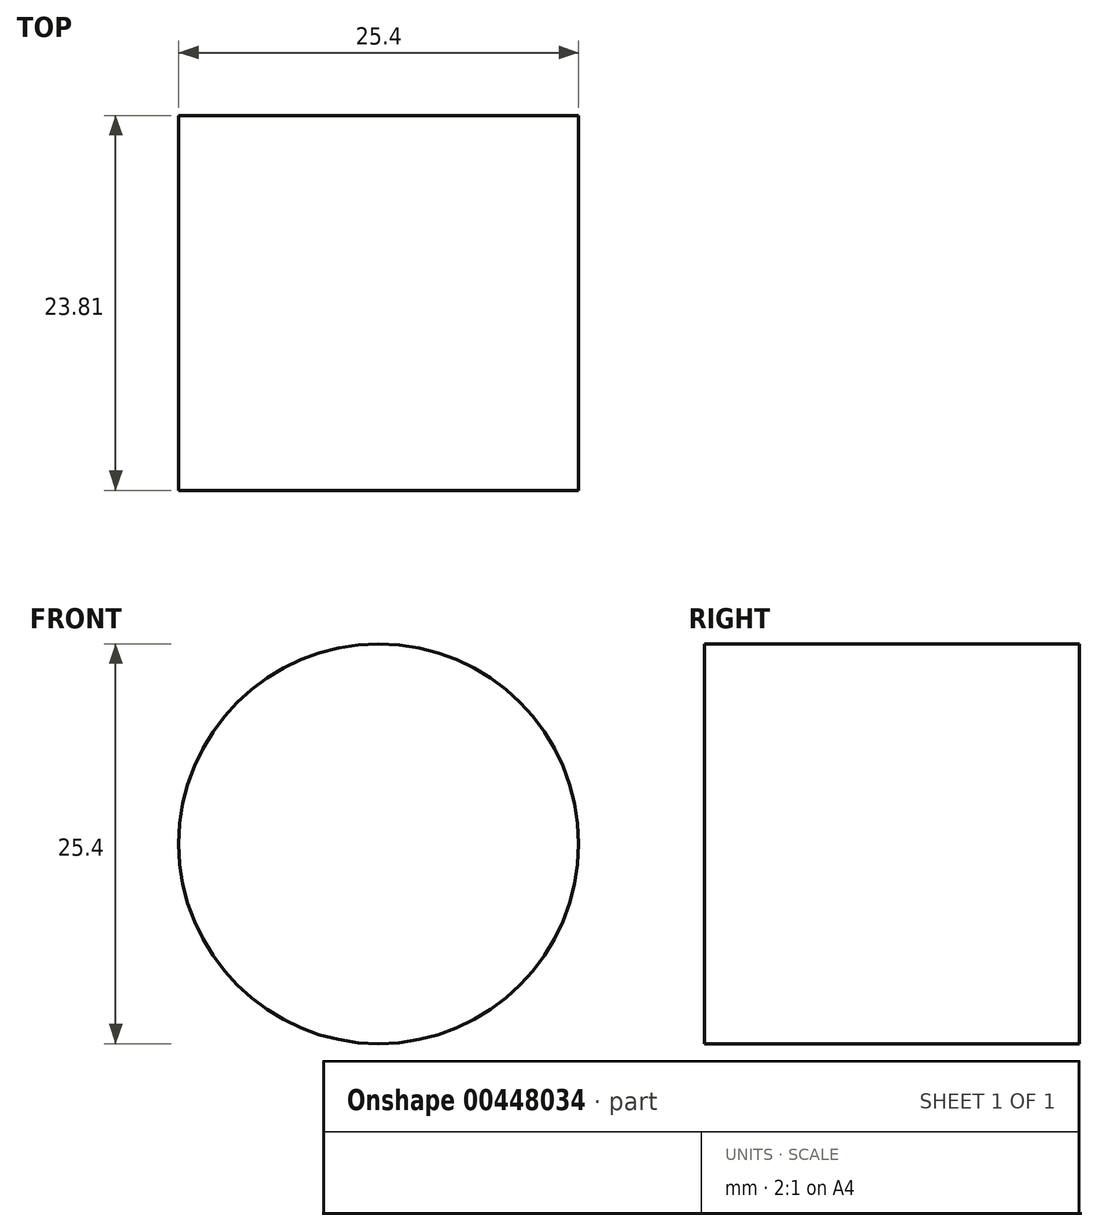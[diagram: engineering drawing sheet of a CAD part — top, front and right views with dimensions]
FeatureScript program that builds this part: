
annotation { "Feature Type Name" : "Feature", "Feature Type Description" : "" }
export const myFeature = defineFeature(function(context is Context, id is Id, definition is map)
    precondition{}
    {
        {
            var Q0;
            Q0=qCreatedBy(makeId("Front.planeOp"),FACE);
            var sketch = newSketch(context, id + "F0", { "sketchPlane" : qUnion([Q0])});
            skCircle(sketch, "E0", {"center": v(0, 0) * mm, "radius": 12.7 * mm});
            skSolve(sketch);
        }
        {
            var Q0;
            Q0=sQuery(id+"FQL6pKlaiTepUYE_0.wireOp",EDGE,"neET6lpr-vOJj-ZEhj-Nltt-b9XqgsA7gR0i");
            var Q1;
            Q1=sQuery(id+"F0.wireOp",EDGE,"E0");
            extrude(context, id + "F1", {"bodyType" : ToolBodyType.SURFACE, "surfaceEntities" : qUnion([Q0, Q1]), "depth" : 23.8 * mm});
        }
    });
